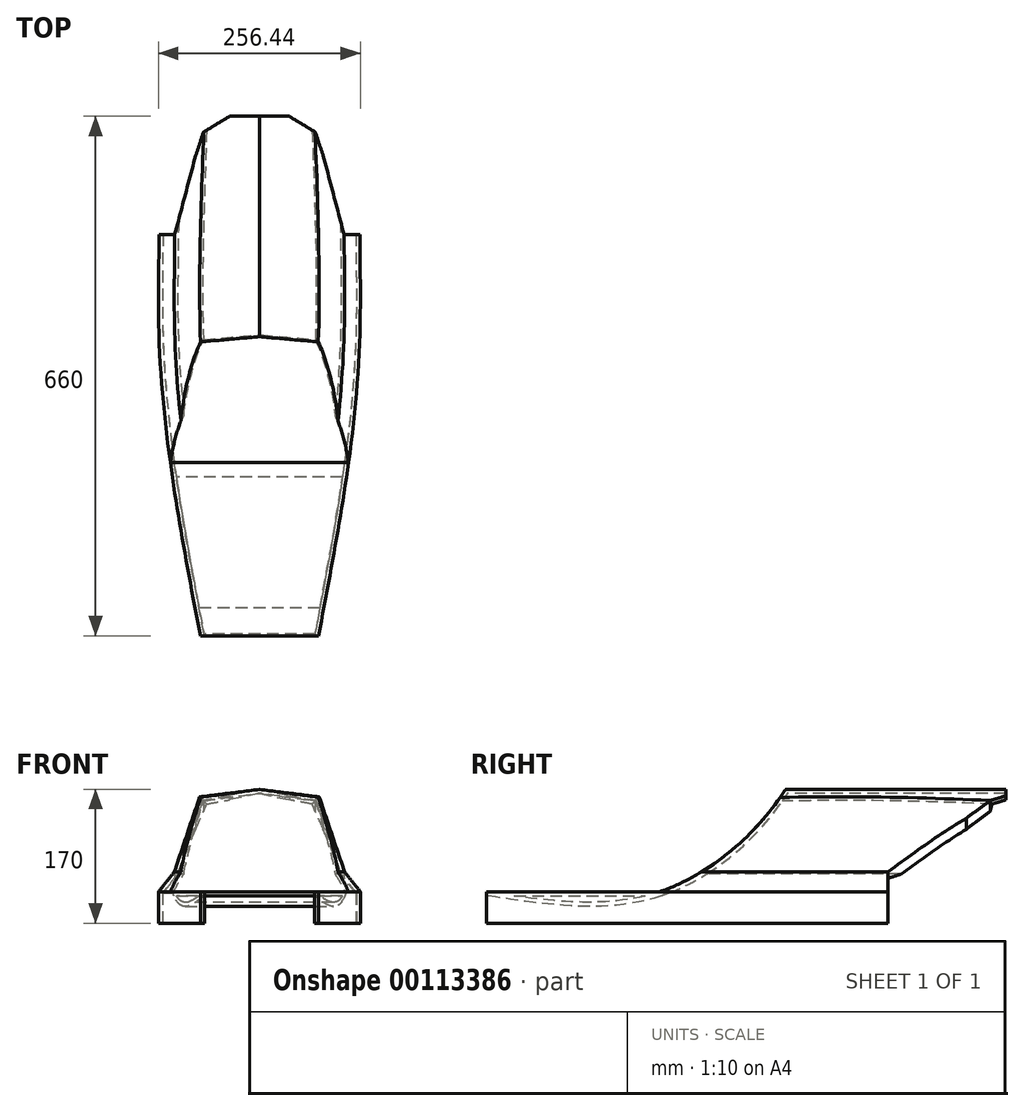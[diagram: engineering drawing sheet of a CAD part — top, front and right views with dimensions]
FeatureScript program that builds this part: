
annotation { "Feature Type Name" : "Feature", "Feature Type Description" : "" }
export const myFeature = defineFeature(function(context is Context, id is Id, definition is map)
    precondition{}
    {
        {
            var Q0;
            Q0=qCreatedBy(makeId("Front.planeOp"),FACE);
            cPlane(context, id + "F0", {"entities" : qUnion([Q0]), "cplaneType" : CPlaneType.OFFSET, "offset" : 380 * mm, "oppositeDirection" : true, "width" : 150 * mm, "height" : 150 * mm});
        }
        {
            var Q0;
            Q0=qCreatedBy(id+"F0.planeOp",FACE);
            cPlane(context, id + "F1", {"entities" : qUnion([Q0]), "cplaneType" : CPlaneType.OFFSET, "offset" : 130 * mm, "oppositeDirection" : true, "width" : 150 * mm, "height" : 150 * mm});
        }
        {
            var Q0;
            Q0=qCreatedBy(id+"F1.planeOp",FACE);
            cPlane(context, id + "F2", {"entities" : qUnion([Q0]), "cplaneType" : CPlaneType.OFFSET, "offset" : 150 * mm, "oppositeDirection" : true, "width" : 150 * mm, "height" : 150 * mm});
        }
        {
            var Q0;
            Q0=qCreatedBy(id+"F2.planeOp",FACE);
            var sketch = newSketch(context, id + "F3", { "sketchPlane" : qUnion([Q0])});
            skLineSegment(sketch, "E0.bottom", {"start": v(0, 0) * mm, "end": v(-127.5, 0) * mm, "construction": true});
            skLineSegment(sketch, "E0.top", {"start": v(0, 170) * mm, "end": v(-127.5, 170) * mm, "construction": true});
            skLineSegment(sketch, "E0.left", {"start": v(0, 0) * mm, "end": v(0, 170) * mm, "construction": true});
            skLineSegment(sketch, "E0.right", {"start": v(-127.5, 0) * mm, "end": v(-127.5, 170) * mm, "construction": true});
            skLineSegment(sketch, "E1.bottom", {"start": v(0, 170) * mm, "end": v(-70, 170) * mm, "construction": true});
            skLineSegment(sketch, "E1.top", {"start": v(0, 155) * mm, "end": v(-70, 155) * mm, "construction": true});
            skLineSegment(sketch, "E1.left", {"start": v(0, 170) * mm, "end": v(0, 155) * mm, "construction": true});
            skLineSegment(sketch, "E1.right", {"start": v(-70, 170) * mm, "end": v(-70, 155) * mm, "construction": true});
            skLineSegment(sketch, "E2.bottom", {"start": v(-127.5, 0) * mm, "end": v(-107.5, 0) * mm, "construction": true});
            skLineSegment(sketch, "E2.top", {"start": v(-127.5, 40) * mm, "end": v(-107.5, 40) * mm, "construction": true});
            skLineSegment(sketch, "E2.left", {"start": v(-127.5, 0) * mm, "end": v(-127.5, 40) * mm, "construction": true});
            skLineSegment(sketch, "E2.right", {"start": v(-107.5, 0) * mm, "end": v(-107.5, 40) * mm, "construction": true});
            skLineSegment(sketch, "E3.bottom", {"start": v(-107.5, 40) * mm, "end": v(-87.5, 40) * mm, "construction": true});
            skLineSegment(sketch, "E3.top", {"start": v(-107.5, 65) * mm, "end": v(-87.5, 65) * mm, "construction": true});
            skLineSegment(sketch, "E3.left", {"start": v(-107.5, 40) * mm, "end": v(-107.5, 65) * mm, "construction": true});
            skLineSegment(sketch, "E3.right", {"start": v(-87.5, 40) * mm, "end": v(-87.5, 65) * mm, "construction": true});
            skLineSegment(sketch, "E4", {"start": v(0, 170) * mm, "end": v(-70, 155) * mm});
            skLineSegment(sketch, "E5", {"start": v(-70, 155) * mm, "end": v(-107.5, 65) * mm});
            skLineSegment(sketch, "E6", {"start": v(-107.5, 65) * mm, "end": v(-127.5, 40) * mm});
            skLineSegment(sketch, "E7", {"start": v(-127.5, 40) * mm, "end": v(-127.5, 0) * mm});
            skLineSegment(sketch, "E8.MirrorCS", {"start": v(127.5, 0) * mm, "end": v(107.5, 0) * mm, "construction": true});
            skLineSegment(sketch, "E9.MirrorCS", {"start": v(127.5, 0) * mm, "end": v(127.5, 40) * mm, "construction": true});
            skLineSegment(sketch, "E10.MirrorCS", {"start": v(70, 170) * mm, "end": v(70, 155) * mm, "construction": true});
            skLineSegment(sketch, "E11.MirrorCS", {"start": v(0, 155) * mm, "end": v(70, 155) * mm, "construction": true});
            skLineSegment(sketch, "E12.MirrorCS", {"start": v(0, 170) * mm, "end": v(70, 170) * mm, "construction": true});
            skLineSegment(sketch, "E13.MirrorCS", {"start": v(127.5, 40) * mm, "end": v(107.5, 40) * mm, "construction": true});
            skLineSegment(sketch, "E14.MirrorCS", {"start": v(127.5, 0) * mm, "end": v(127.5, 170) * mm, "construction": true});
            skLineSegment(sketch, "E15.MirrorCS", {"start": v(0, 170) * mm, "end": v(127.5, 170) * mm, "construction": true});
            skLineSegment(sketch, "E16.MirrorCS", {"start": v(0, 0) * mm, "end": v(127.5, 0) * mm, "construction": true});
            skLineSegment(sketch, "E17.MirrorCS", {"start": v(87.5, 40) * mm, "end": v(87.5, 65) * mm, "construction": true});
            skLineSegment(sketch, "E18.MirrorCS", {"start": v(127.5, 40) * mm, "end": v(127.5, 0) * mm});
            skLineSegment(sketch, "E19.MirrorCS", {"start": v(107.5, 0) * mm, "end": v(107.5, 40) * mm, "construction": true});
            skLineSegment(sketch, "E20.MirrorCS", {"start": v(107.5, 40) * mm, "end": v(87.5, 40) * mm, "construction": true});
            skLineSegment(sketch, "E21.MirrorCS", {"start": v(0, 170) * mm, "end": v(70, 155) * mm});
            skLineSegment(sketch, "E22.MirrorCS", {"start": v(107.5, 40) * mm, "end": v(107.5, 65) * mm, "construction": true});
            skLineSegment(sketch, "E23.MirrorCS", {"start": v(107.5, 65) * mm, "end": v(87.5, 65) * mm, "construction": true});
            skLineSegment(sketch, "E24.MirrorCS", {"start": v(70, 155) * mm, "end": v(107.5, 65) * mm});
            skLineSegment(sketch, "E25.MirrorCS", {"start": v(107.5, 65) * mm, "end": v(127.5, 40) * mm});
            skLineSegment(sketch, "E26.0", {"start": v(122.5, 38.25) * mm, "end": v(122.5, 0) * mm});
            skLineSegment(sketch, "E26.1", {"start": v(103.16, 62.43) * mm, "end": v(122.5, 38.25) * mm});
            skLineSegment(sketch, "E26.2", {"start": v(66.4, 150.66) * mm, "end": v(103.16, 62.43) * mm});
            skLineSegment(sketch, "E26.3", {"start": v(0, 164.89) * mm, "end": v(66.4, 150.66) * mm});
            skLineSegment(sketch, "E26.4", {"start": v(-122.5, 38.25) * mm, "end": v(-122.5, 0) * mm});
            skLineSegment(sketch, "E26.5", {"start": v(-103.16, 62.43) * mm, "end": v(-122.5, 38.25) * mm});
            skLineSegment(sketch, "E26.6", {"start": v(-66.4, 150.66) * mm, "end": v(-103.16, 62.43) * mm});
            skLineSegment(sketch, "E26.7", {"start": v(0, 164.89) * mm, "end": v(-66.4, 150.66) * mm});
            skLineSegment(sketch, "E27", {"start": v(127.5, 0) * mm, "end": v(122.5, 0) * mm});
            skLineSegment(sketch, "E28", {"start": v(-122.5, 0) * mm, "end": v(-127.5, 0) * mm});
            skSolve(sketch);
        }
        {
            var Q0;
            Q0=qCreatedBy(id+"F1.planeOp",FACE);
            var sketch = newSketch(context, id + "F4", { "sketchPlane" : qUnion([Q0])});
            skLineSegment(sketch, "E29.bottom", {"start": v(0, 0) * mm, "end": v(-127.5, 0) * mm, "construction": true});
            skLineSegment(sketch, "E29.top", {"start": v(0, 170) * mm, "end": v(-127.5, 170) * mm, "construction": true});
            skLineSegment(sketch, "E29.left", {"start": v(0, 0) * mm, "end": v(0, 170) * mm, "construction": true});
            skLineSegment(sketch, "E29.right", {"start": v(-127.5, 0) * mm, "end": v(-127.5, 170) * mm, "construction": true});
            skLineSegment(sketch, "E30.bottom", {"start": v(0, 170) * mm, "end": v(-75, 170) * mm, "construction": true});
            skLineSegment(sketch, "E30.top", {"start": v(0, 160) * mm, "end": v(-75, 160) * mm, "construction": true});
            skLineSegment(sketch, "E30.left", {"start": v(0, 170) * mm, "end": v(0, 160) * mm, "construction": true});
            skLineSegment(sketch, "E30.right", {"start": v(-75, 170) * mm, "end": v(-75, 160) * mm, "construction": true});
            skLineSegment(sketch, "E31.bottom", {"start": v(-127.5, 0) * mm, "end": v(-107.5, 0) * mm, "construction": true});
            skLineSegment(sketch, "E31.top", {"start": v(-127.5, 40) * mm, "end": v(-107.5, 40) * mm, "construction": true});
            skLineSegment(sketch, "E31.left", {"start": v(-127.5, 0) * mm, "end": v(-127.5, 40) * mm, "construction": true});
            skLineSegment(sketch, "E31.right", {"start": v(-107.5, 0) * mm, "end": v(-107.5, 40) * mm, "construction": true});
            skLineSegment(sketch, "E32.bottom", {"start": v(-107.5, 40) * mm, "end": v(-87.5, 40) * mm, "construction": true});
            skLineSegment(sketch, "E32.top", {"start": v(-107.5, 65) * mm, "end": v(-87.5, 65) * mm, "construction": true});
            skLineSegment(sketch, "E32.left", {"start": v(-107.5, 40) * mm, "end": v(-107.5, 65) * mm, "construction": true});
            skLineSegment(sketch, "E32.right", {"start": v(-87.5, 40) * mm, "end": v(-87.5, 65) * mm, "construction": true});
            skLineSegment(sketch, "E33", {"start": v(0, 170) * mm, "end": v(-75, 160) * mm});
            skLineSegment(sketch, "E34", {"start": v(-75, 160) * mm, "end": v(-107.5, 65) * mm});
            skLineSegment(sketch, "E35", {"start": v(-107.5, 65) * mm, "end": v(-127.5, 40) * mm});
            skLineSegment(sketch, "E36", {"start": v(-127.5, 40) * mm, "end": v(-127.5, 0) * mm});
            skLineSegment(sketch, "E37.MirrorCS", {"start": v(127.5, 0) * mm, "end": v(107.5, 0) * mm, "construction": true});
            skLineSegment(sketch, "E38.MirrorCS", {"start": v(127.5, 0) * mm, "end": v(127.5, 40) * mm, "construction": true});
            skLineSegment(sketch, "E39.MirrorCS", {"start": v(75, 170) * mm, "end": v(75, 160) * mm, "construction": true});
            skLineSegment(sketch, "E40.MirrorCS", {"start": v(0, 160) * mm, "end": v(75, 160) * mm, "construction": true});
            skLineSegment(sketch, "E41.MirrorCS", {"start": v(0, 170) * mm, "end": v(75, 170) * mm, "construction": true});
            skLineSegment(sketch, "E42.MirrorCS", {"start": v(127.5, 40) * mm, "end": v(107.5, 40) * mm, "construction": true});
            skLineSegment(sketch, "E43.MirrorCS", {"start": v(127.5, 0) * mm, "end": v(127.5, 170) * mm, "construction": true});
            skLineSegment(sketch, "E44.MirrorCS", {"start": v(0, 170) * mm, "end": v(127.5, 170) * mm, "construction": true});
            skLineSegment(sketch, "E45.MirrorCS", {"start": v(0, 0) * mm, "end": v(127.5, 0) * mm, "construction": true});
            skLineSegment(sketch, "E46.MirrorCS", {"start": v(87.5, 40) * mm, "end": v(87.5, 65) * mm, "construction": true});
            skLineSegment(sketch, "E47.MirrorCS", {"start": v(127.5, 40) * mm, "end": v(127.5, 0) * mm});
            skLineSegment(sketch, "E48.MirrorCS", {"start": v(107.5, 0) * mm, "end": v(107.5, 40) * mm, "construction": true});
            skLineSegment(sketch, "E49.MirrorCS", {"start": v(107.5, 40) * mm, "end": v(87.5, 40) * mm, "construction": true});
            skLineSegment(sketch, "E50.MirrorCS", {"start": v(0, 170) * mm, "end": v(75, 160) * mm});
            skLineSegment(sketch, "E51.MirrorCS", {"start": v(107.5, 40) * mm, "end": v(107.5, 65) * mm, "construction": true});
            skLineSegment(sketch, "E52.MirrorCS", {"start": v(107.5, 65) * mm, "end": v(87.5, 65) * mm, "construction": true});
            skLineSegment(sketch, "E53.MirrorCS", {"start": v(75, 160) * mm, "end": v(107.5, 65) * mm});
            skLineSegment(sketch, "E54.MirrorCS", {"start": v(107.5, 65) * mm, "end": v(127.5, 40) * mm});
            skLineSegment(sketch, "E55.0", {"start": v(122.5, 38.25) * mm, "end": v(122.5, 0) * mm});
            skLineSegment(sketch, "E55.1", {"start": v(103.05, 62.56) * mm, "end": v(122.5, 38.25) * mm});
            skLineSegment(sketch, "E55.2", {"start": v(71.27, 155.45) * mm, "end": v(103.05, 62.56) * mm});
            skLineSegment(sketch, "E55.3", {"start": v(0, 164.96) * mm, "end": v(71.27, 155.45) * mm});
            skLineSegment(sketch, "E55.4", {"start": v(-122.5, 38.25) * mm, "end": v(-122.5, 0) * mm});
            skLineSegment(sketch, "E55.5", {"start": v(-103.05, 62.56) * mm, "end": v(-122.5, 38.25) * mm});
            skLineSegment(sketch, "E55.6", {"start": v(-71.27, 155.45) * mm, "end": v(-103.05, 62.56) * mm});
            skLineSegment(sketch, "E55.7", {"start": v(0, 164.96) * mm, "end": v(-71.27, 155.45) * mm});
            skLineSegment(sketch, "E56", {"start": v(127.5, 0) * mm, "end": v(122.5, 0) * mm});
            skLineSegment(sketch, "E57", {"start": v(-122.5, 0) * mm, "end": v(-127.5, 0) * mm});
            skSolve(sketch);
        }
        {
            var Q0;
            Q0=qCreatedBy(id+"F0.planeOp",FACE);
            var sketch = newSketch(context, id + "F5", { "sketchPlane" : qUnion([Q0])});
            skLineSegment(sketch, "E58.bottom", {"start": v(0, 0) * mm, "end": v(-127.5, 0) * mm, "construction": true});
            skLineSegment(sketch, "E58.top", {"start": v(0, 170) * mm, "end": v(-127.5, 170) * mm, "construction": true});
            skLineSegment(sketch, "E58.left", {"start": v(0, 0) * mm, "end": v(0, 170) * mm, "construction": true});
            skLineSegment(sketch, "E58.right", {"start": v(-127.5, 0) * mm, "end": v(-127.5, 170) * mm, "construction": true});
            skLineSegment(sketch, "E59.bottom", {"start": v(0, 170) * mm, "end": v(-75, 170) * mm, "construction": true});
            skLineSegment(sketch, "E59.top", {"start": v(0, 160) * mm, "end": v(-75, 160) * mm, "construction": true});
            skLineSegment(sketch, "E59.left", {"start": v(0, 170) * mm, "end": v(0, 160) * mm, "construction": true});
            skLineSegment(sketch, "E59.right", {"start": v(-75, 170) * mm, "end": v(-75, 160) * mm, "construction": true});
            skLineSegment(sketch, "E60.bottom", {"start": v(-127.5, 0) * mm, "end": v(-107.5, 0) * mm, "construction": true});
            skLineSegment(sketch, "E60.top", {"start": v(-127.5, 40) * mm, "end": v(-107.5, 40) * mm, "construction": true});
            skLineSegment(sketch, "E60.left", {"start": v(-127.5, 0) * mm, "end": v(-127.5, 40) * mm, "construction": true});
            skLineSegment(sketch, "E60.right", {"start": v(-107.5, 0) * mm, "end": v(-107.5, 40) * mm, "construction": true});
            skLineSegment(sketch, "E61.bottom", {"start": v(-107.5, 40) * mm, "end": v(-87.5, 40) * mm, "construction": true});
            skLineSegment(sketch, "E61.top", {"start": v(-107.5, 65) * mm, "end": v(-87.5, 65) * mm, "construction": true});
            skLineSegment(sketch, "E61.left", {"start": v(-107.5, 40) * mm, "end": v(-107.5, 65) * mm, "construction": true});
            skLineSegment(sketch, "E61.right", {"start": v(-87.5, 40) * mm, "end": v(-87.5, 65) * mm, "construction": true});
            skLineSegment(sketch, "E62", {"start": v(0, 170) * mm, "end": v(-75, 160) * mm});
            skLineSegment(sketch, "E63", {"start": v(-75, 160) * mm, "end": v(-107.5, 65) * mm});
            skLineSegment(sketch, "E64", {"start": v(-107.5, 65) * mm, "end": v(-127.5, 40) * mm});
            skLineSegment(sketch, "E65", {"start": v(-127.5, 40) * mm, "end": v(-127.5, 0) * mm});
            skLineSegment(sketch, "E66.MirrorCS", {"start": v(127.5, 0) * mm, "end": v(107.5, 0) * mm, "construction": true});
            skLineSegment(sketch, "E67.MirrorCS", {"start": v(127.5, 0) * mm, "end": v(127.5, 40) * mm, "construction": true});
            skLineSegment(sketch, "E68.MirrorCS", {"start": v(75, 170) * mm, "end": v(75, 160) * mm, "construction": true});
            skLineSegment(sketch, "E69.MirrorCS", {"start": v(0, 160) * mm, "end": v(75, 160) * mm, "construction": true});
            skLineSegment(sketch, "E70.MirrorCS", {"start": v(0, 170) * mm, "end": v(75, 170) * mm, "construction": true});
            skLineSegment(sketch, "E71.MirrorCS", {"start": v(127.5, 40) * mm, "end": v(107.5, 40) * mm, "construction": true});
            skLineSegment(sketch, "E72.MirrorCS", {"start": v(127.5, 0) * mm, "end": v(127.5, 170) * mm, "construction": true});
            skLineSegment(sketch, "E73.MirrorCS", {"start": v(0, 170) * mm, "end": v(127.5, 170) * mm, "construction": true});
            skLineSegment(sketch, "E74.MirrorCS", {"start": v(0, 0) * mm, "end": v(127.5, 0) * mm, "construction": true});
            skLineSegment(sketch, "E75.MirrorCS", {"start": v(87.5, 40) * mm, "end": v(87.5, 65) * mm, "construction": true});
            skLineSegment(sketch, "E76.MirrorCS", {"start": v(127.5, 40) * mm, "end": v(127.5, 0) * mm});
            skLineSegment(sketch, "E77.MirrorCS", {"start": v(107.5, 0) * mm, "end": v(107.5, 40) * mm, "construction": true});
            skLineSegment(sketch, "E78.MirrorCS", {"start": v(107.5, 40) * mm, "end": v(87.5, 40) * mm, "construction": true});
            skLineSegment(sketch, "E79.MirrorCS", {"start": v(0, 170) * mm, "end": v(75, 160) * mm});
            skLineSegment(sketch, "E80.MirrorCS", {"start": v(107.5, 40) * mm, "end": v(107.5, 65) * mm, "construction": true});
            skLineSegment(sketch, "E81.MirrorCS", {"start": v(107.5, 65) * mm, "end": v(87.5, 65) * mm, "construction": true});
            skLineSegment(sketch, "E82.MirrorCS", {"start": v(75, 160) * mm, "end": v(107.5, 65) * mm});
            skLineSegment(sketch, "E83.MirrorCS", {"start": v(107.5, 65) * mm, "end": v(127.5, 40) * mm});
            skLineSegment(sketch, "E84.0", {"start": v(122.5, 38.25) * mm, "end": v(122.5, 0) * mm});
            skLineSegment(sketch, "E84.1", {"start": v(103.05, 62.56) * mm, "end": v(122.5, 38.25) * mm});
            skLineSegment(sketch, "E84.2", {"start": v(71.27, 155.45) * mm, "end": v(103.05, 62.56) * mm});
            skLineSegment(sketch, "E84.3", {"start": v(0, 164.96) * mm, "end": v(71.27, 155.45) * mm});
            skLineSegment(sketch, "E84.4", {"start": v(-122.5, 38.25) * mm, "end": v(-122.5, 0) * mm});
            skLineSegment(sketch, "E84.5", {"start": v(-103.05, 62.56) * mm, "end": v(-122.5, 38.25) * mm});
            skLineSegment(sketch, "E84.6", {"start": v(-71.27, 155.45) * mm, "end": v(-103.05, 62.56) * mm});
            skLineSegment(sketch, "E84.7", {"start": v(0, 164.96) * mm, "end": v(-71.27, 155.45) * mm});
            skLineSegment(sketch, "E85", {"start": v(127.5, 0) * mm, "end": v(122.5, 0) * mm});
            skLineSegment(sketch, "E86", {"start": v(-122.5, 0) * mm, "end": v(-127.5, 0) * mm});
            skSolve(sketch);
        }
        {
            var Q0;
            Q0=qCreatedBy(makeId("Front.planeOp"),FACE);
            var sketch = newSketch(context, id + "F6", { "sketchPlane" : qUnion([Q0])});
            skLineSegment(sketch, "E87.bottom", {"start": v(0, 0) * mm, "end": v(-75, 0) * mm, "construction": true});
            skLineSegment(sketch, "E87.top", {"start": v(0, 170) * mm, "end": v(-75, 170) * mm, "construction": true});
            skLineSegment(sketch, "E87.left", {"start": v(0, 0) * mm, "end": v(0, 170) * mm, "construction": true});
            skLineSegment(sketch, "E87.right", {"start": v(-75, 0) * mm, "end": v(-75, 170) * mm, "construction": true});
            skLineSegment(sketch, "E88.bottom", {"start": v(0, 170) * mm, "end": v(-30, 170) * mm, "construction": true});
            skLineSegment(sketch, "E88.top", {"start": v(0, 160) * mm, "end": v(-30, 160) * mm, "construction": true});
            skLineSegment(sketch, "E88.left", {"start": v(0, 170) * mm, "end": v(0, 160) * mm, "construction": true});
            skLineSegment(sketch, "E88.right", {"start": v(-30, 170) * mm, "end": v(-30, 160) * mm, "construction": true});
            skLineSegment(sketch, "E89.bottom", {"start": v(-75, 0) * mm, "end": v(-55, 0) * mm, "construction": true});
            skLineSegment(sketch, "E89.top", {"start": v(-75, 40) * mm, "end": v(-55, 40) * mm, "construction": true});
            skLineSegment(sketch, "E89.left", {"start": v(-75, 0) * mm, "end": v(-75, 40) * mm, "construction": true});
            skLineSegment(sketch, "E89.right", {"start": v(-55, 0) * mm, "end": v(-55, 40) * mm, "construction": true});
            skLineSegment(sketch, "E90.bottom", {"start": v(-55, 40) * mm, "end": v(-35, 40) * mm, "construction": true});
            skLineSegment(sketch, "E90.top", {"start": v(-55, 65) * mm, "end": v(-35, 65) * mm, "construction": true});
            skLineSegment(sketch, "E90.left", {"start": v(-55, 40) * mm, "end": v(-55, 65) * mm, "construction": true});
            skLineSegment(sketch, "E90.right", {"start": v(-35, 40) * mm, "end": v(-35, 65) * mm, "construction": true});
            skLineSegment(sketch, "E91", {"start": v(0, 170) * mm, "end": v(-30, 160) * mm});
            skLineSegment(sketch, "E92", {"start": v(-30, 160) * mm, "end": v(-55, 65) * mm});
            skLineSegment(sketch, "E93", {"start": v(-55, 65) * mm, "end": v(-75, 40) * mm});
            skLineSegment(sketch, "E94", {"start": v(-75, 40) * mm, "end": v(-75, 0) * mm});
            skLineSegment(sketch, "E95.MirrorCS", {"start": v(75, 0) * mm, "end": v(55, 0) * mm, "construction": true});
            skLineSegment(sketch, "E96.MirrorCS", {"start": v(75, 0) * mm, "end": v(75, 40) * mm, "construction": true});
            skLineSegment(sketch, "E97.MirrorCS", {"start": v(30, 170) * mm, "end": v(30, 160) * mm, "construction": true});
            skLineSegment(sketch, "E98.MirrorCS", {"start": v(0, 160) * mm, "end": v(30, 160) * mm, "construction": true});
            skLineSegment(sketch, "E99.MirrorCS", {"start": v(0, 170) * mm, "end": v(30, 170) * mm, "construction": true});
            skLineSegment(sketch, "E100.MirrorCS", {"start": v(75, 40) * mm, "end": v(55, 40) * mm, "construction": true});
            skLineSegment(sketch, "E101.MirrorCS", {"start": v(75, 0) * mm, "end": v(75, 170) * mm, "construction": true});
            skLineSegment(sketch, "E102.MirrorCS", {"start": v(0, 170) * mm, "end": v(75, 170) * mm, "construction": true});
            skLineSegment(sketch, "E103.MirrorCS", {"start": v(0, 0) * mm, "end": v(75, 0) * mm, "construction": true});
            skLineSegment(sketch, "E104.MirrorCS", {"start": v(35, 40) * mm, "end": v(35, 65) * mm, "construction": true});
            skLineSegment(sketch, "E105.MirrorCS", {"start": v(75, 40) * mm, "end": v(75, 0) * mm});
            skLineSegment(sketch, "E106.MirrorCS", {"start": v(55, 0) * mm, "end": v(55, 40) * mm, "construction": true});
            skLineSegment(sketch, "E107.MirrorCS", {"start": v(55, 40) * mm, "end": v(35, 40) * mm, "construction": true});
            skLineSegment(sketch, "E108.MirrorCS", {"start": v(0, 170) * mm, "end": v(30, 160) * mm});
            skLineSegment(sketch, "E109.MirrorCS", {"start": v(55, 40) * mm, "end": v(55, 65) * mm, "construction": true});
            skLineSegment(sketch, "E110.MirrorCS", {"start": v(55, 65) * mm, "end": v(35, 65) * mm, "construction": true});
            skLineSegment(sketch, "E111.MirrorCS", {"start": v(30, 160) * mm, "end": v(55, 65) * mm});
            skLineSegment(sketch, "E112.MirrorCS", {"start": v(55, 65) * mm, "end": v(75, 40) * mm});
            skLineSegment(sketch, "E113.0", {"start": v(70, 38.25) * mm, "end": v(70, 0) * mm});
            skLineSegment(sketch, "E113.1", {"start": v(50.43, 62.7) * mm, "end": v(70, 38.25) * mm});
            skLineSegment(sketch, "E113.2", {"start": v(25.85, 156.11) * mm, "end": v(50.43, 62.7) * mm});
            skLineSegment(sketch, "E113.3", {"start": v(0, 164.73) * mm, "end": v(25.85, 156.11) * mm});
            skLineSegment(sketch, "E113.4", {"start": v(-70, 38.25) * mm, "end": v(-70, 0) * mm});
            skLineSegment(sketch, "E113.5", {"start": v(-50.43, 62.7) * mm, "end": v(-70, 38.25) * mm});
            skLineSegment(sketch, "E113.6", {"start": v(-25.85, 156.11) * mm, "end": v(-50.43, 62.7) * mm});
            skLineSegment(sketch, "E113.7", {"start": v(0, 164.73) * mm, "end": v(-25.85, 156.11) * mm});
            skLineSegment(sketch, "E114", {"start": v(75, 0) * mm, "end": v(70, 0) * mm});
            skLineSegment(sketch, "E115", {"start": v(-70, 0) * mm, "end": v(-75, 0) * mm});
            skSolve(sketch);
        }
        {
            var Q0;
            Q0=qCreatedBy(makeId("Right.planeOp"),FACE);
            var sketch = newSketch(context, id + "F7", { "sketchPlane" : qUnion([Q0])});
            skLineSegment(sketch, "E116", {"start": v(0, 0) * mm, "end": v(380, 0) * mm, "construction": true});
            skLineSegment(sketch, "E117", {"start": v(380, 0) * mm, "end": v(380, 170) * mm, "construction": true});
            skLineSegment(sketch, "E118", {"start": v(0, 0) * mm, "end": v(0, 40) * mm, "construction": true});
            skLineSegment(sketch, "E119", {"start": v(0, 40) * mm, "end": v(220, 40) * mm});
            skFitSpline(sketch, "E120", {"points": [v(380, 170) * mm, v(220, 40) * mm, v(0, 40) * mm], "startDerivative": vector(-215.96, -343.22) * mm, "endDerivative": vector(-478.3, 74.11) * mm});
            skLineSegment(sketch, "E121", {"start": v(380, 170) * mm, "end": v(380, 230.78) * mm});
            skLineSegment(sketch, "E122", {"start": v(380, 230.78) * mm, "end": v(7.34, 230.78) * mm});
            skLineSegment(sketch, "E123", {"start": v(7.34, 230.78) * mm, "end": v(-5.55, 185.11) * mm});
            skLineSegment(sketch, "E124", {"start": v(-5.55, 185.11) * mm, "end": v(0, 40) * mm});
            skSolve(sketch);
        }
        {
            var Q0;
            Q0=qCreatedBy(makeId("Right.planeOp"),FACE);
            var sketch = newSketch(context, id + "F8", { "sketchPlane" : qUnion([Q0])});
            skLineSegment(sketch, "E125", {"start": v(0, 0) * mm, "end": v(600, 0) * mm, "construction": true});
            skLineSegment(sketch, "E126", {"start": v(600, 0) * mm, "end": v(600, 40) * mm});
            skLineSegment(sketch, "E127", {"start": v(600, 40) * mm, "end": v(600, 65) * mm, "construction": true});
            skLineSegment(sketch, "E128", {"start": v(600, 65) * mm, "end": v(625, 65) * mm, "construction": true});
            skLineSegment(sketch, "E129", {"start": v(600, 40) * mm, "end": v(625, 65) * mm});
            skLineSegment(sketch, "E130", {"start": v(625, 65) * mm, "end": v(880.62, 212.2) * mm});
            skLineSegment(sketch, "E131", {"start": v(880.62, 212.2) * mm, "end": v(932.67, 242.1) * mm});
            skLineSegment(sketch, "E132", {"start": v(932.67, 242.1) * mm, "end": v(866.28, 117.59) * mm});
            skLineSegment(sketch, "E133", {"start": v(866.28, 117.59) * mm, "end": v(834.8, 61.75) * mm});
            skLineSegment(sketch, "E134", {"start": v(600, 0) * mm, "end": v(790, 0) * mm});
            skLineSegment(sketch, "E135", {"start": v(790, 0) * mm, "end": v(790, 65) * mm, "construction": true});
            skLineSegment(sketch, "E136", {"start": v(834.8, 61.75) * mm, "end": v(790, 0) * mm});
            skSolve(sketch);
        }
        {
            var Q0;
            Q0=qCreatedBy(makeId("Right.planeOp"),FACE);
            var sketch = newSketch(context, id + "F9", { "sketchPlane" : qUnion([Q0])});
            skLineSegment(sketch, "E137", {"start": v(0, 0) * mm, "end": v(380, 0) * mm, "construction": true});
            skLineSegment(sketch, "E138", {"start": v(380, 0) * mm, "end": v(380, 170) * mm, "construction": true});
            skLineSegment(sketch, "E139", {"start": v(0, 0) * mm, "end": v(0, 40) * mm, "construction": true});
            skLineSegment(sketch, "E140", {"start": v(0, 40) * mm, "end": v(220, 40) * mm});
            skFitSpline(sketch, "E141", {"points": [v(380, 170) * mm, v(220, 40) * mm, v(0, 40) * mm], "startDerivative": vector(-215.96, -343.22) * mm, "endDerivative": vector(-478.3, 74.11) * mm});
            skLineSegment(sketch, "E142", {"start": v(2.2, -5.3) * mm, "end": v(382.2, -5.3) * mm, "construction": true});
            skLineSegment(sketch, "E143", {"start": v(382.2, -5.3) * mm, "end": v(382.2, 164.7) * mm, "construction": true});
            skLineSegment(sketch, "E144", {"start": v(2.2, -5.3) * mm, "end": v(2.2, 34.7) * mm, "construction": true});
            skLineSegment(sketch, "E145", {"start": v(2.2, 34.7) * mm, "end": v(222.2, 34.7) * mm});
            skFitSpline(sketch, "E146", {"points": [v(382.2, 164.7) * mm, v(222.2, 34.7) * mm, v(2.2, 34.7) * mm], "startDerivative": vector(-215.96, -343.22) * mm, "endDerivative": vector(-478.3, 74.11) * mm});
            skLineSegment(sketch, "E147", {"start": v(2.2, 34.7) * mm, "end": v(0, 40) * mm});
            skLineSegment(sketch, "E148", {"start": v(382.2, 164.7) * mm, "end": v(380, 170) * mm});
            skSolve(sketch);
        }
        {
            var Q0;
            Q0 = qSketchRegion(id + "F3", true);
            var Q1;
            Q1 = qSketchRegion(id + "F4", true);
            var Q2;
            Q2 = qSketchRegion(id + "F5", true);
            var Q3;
            Q3 = qSketchRegion(id + "F6", true);
            loft(context, id + "F10", {"sheetProfilesArray" : [{ "sheetProfileEntities" : qUnion([Q0]) }, { "sheetProfileEntities" : qUnion([Q1]) }, { "sheetProfileEntities" : qUnion([Q2]) }, { "sheetProfileEntities" : qUnion([Q3]) }]});
        }
        {
            var Q0;
            Q0=makeQuery(id+"F7.imprint","IMPRINT",FACE,{"disambiguationData":[TD([[makeQuery(id+"F7.imprint","IMPRINT",EDGE,{"derivedFrom":sQuery(id+"F7.wireOp",EDGE,"E119")}),1.0]])]});
            extrude(context, id + "F11", {"entities" : qUnion([Q0]), "operationType" : NewBodyOperationType.REMOVE, "endBound" : BoundingType.THROUGH_ALL, "oppositeDirection" : true, "depth" : 25 * mm, "hasSecondDirection" : true, "secondDirectionBound" : SecondDirectionBoundingType.THROUGH_ALL, "secondDirectionOppositeDirection" : false, "secondDirectionDepth" : 25 * mm});
        }
        {
            var Q0;
            Q0 = qSketchRegion(id + "F9", true);
            var Q1;
            Q1 = qConstructionFilter(qBodyType(qCreatedBy(id + "F6" ,EDGE), BodyType.WIRE), ConstructionObject.NO);
            var Q2;
            Q2 = qConstructionFilter(qBodyType(qCreatedBy(id + "F5" ,EDGE), BodyType.WIRE), ConstructionObject.NO);
            var Q3;
            Q3 = qConstructionFilter(qBodyType(qCreatedBy(id + "F4" ,EDGE), BodyType.WIRE), ConstructionObject.NO);
            var Q4;
            Q4=makeQuery(id+"F10.opLoft","SWEPT_BODY",BODY,{"disambiguationData":[OSD([makeQuery(id+"F3.imprint","IMPRINT",FACE,{"disambiguationData":[TD([[makeQuery(id+"F3.imprint","IMPRINT",EDGE,{"derivedFrom":sQuery(id+"F3.wireOp",EDGE,"E4")}),1.0]])]}),sQuery(id+"F4.wireOp",EDGE,"E55.7"),sQuery(id+"F5.wireOp",EDGE,"E84.7"),makeQuery(id+"F6.imprint","IMPRINT",FACE,{"disambiguationData":[TD([[makeQuery(id+"F6.imprint","IMPRINT",EDGE,{"derivedFrom":sQuery(id+"F6.wireOp",EDGE,"E91")}),1.0]])]})])]});
            var Q5;
            Q5=makeQuery(id+"F10.opLoft","SWEPT_BODY",BODY,{"disambiguationData":[OSD([makeQuery(id+"F3.imprint","IMPRINT",FACE,{"disambiguationData":[TD([[makeQuery(id+"F3.imprint","IMPRINT",EDGE,{"derivedFrom":sQuery(id+"F3.wireOp",EDGE,"E4")}),1.0]])]}),sQuery(id+"F4.wireOp",EDGE,"E55.7"),sQuery(id+"F5.wireOp",EDGE,"E84.7"),makeQuery(id+"F6.imprint","IMPRINT",FACE,{"disambiguationData":[TD([[makeQuery(id+"F6.imprint","IMPRINT",EDGE,{"derivedFrom":sQuery(id+"F6.wireOp",EDGE,"E91")}),1.0]])]})])]});
            extrude(context, id + "F12", {"entities" : qUnion([Q0]), "operationType" : NewBodyOperationType.ADD, "surfaceEntities" : qUnion([Q1, Q2, Q3]), "endBound" : BoundingType.UP_TO_BODY, "endBoundEntityBody" : qUnion([Q4]), "depth" : 170 * mm, "hasSecondDirection" : true, "secondDirectionBound" : SecondDirectionBoundingType.UP_TO_BODY, "secondDirectionOppositeDirection" : true, "secondDirectionBoundEntityBody" : qUnion([Q5]), "secondDirectionDepth" : 25 * mm});
        }
        {
            var Q0;
            Q0=qCreatedBy(makeId("Top.planeOp"),FACE);
            var sketch = newSketch(context, id + "F13", { "sketchPlane" : qUnion([Q0])});
            skLineSegment(sketch, "E149", {"start": v(0, 0) * mm, "end": v(0, 660) * mm, "construction": true});
            skLineSegment(sketch, "E150", {"start": v(0, 660) * mm, "end": v(-38, 660) * mm, "construction": true});
            skLineSegment(sketch, "E151", {"start": v(0, 640) * mm, "end": v(-71, 640) * mm, "construction": true});
            skLineSegment(sketch, "E152", {"start": v(-38, 660) * mm, "end": v(-71, 640) * mm});
            skLineSegment(sketch, "E153", {"start": v(-71, 640) * mm, "end": v(-71, 610) * mm, "construction": true});
            skLineSegment(sketch, "E154", {"start": v(-71, 610) * mm, "end": v(-81, 610) * mm, "construction": true});
            skLineSegment(sketch, "E155", {"start": v(-71, 640) * mm, "end": v(-81, 610) * mm});
            skLineSegment(sketch, "E156", {"start": v(-81, 610) * mm, "end": v(-81, 605) * mm, "construction": true});
            skLineSegment(sketch, "E157", {"start": v(0, 510) * mm, "end": v(-107.58, 510) * mm, "construction": true});
            skLineSegment(sketch, "E158", {"start": v(-81, 610) * mm, "end": v(-107.58, 510) * mm});
            skLineSegment(sketch, "E159", {"start": v(-107.58, 510) * mm, "end": v(-166.67, 510) * mm});
            skLineSegment(sketch, "E160", {"start": v(-166.67, 510) * mm, "end": v(-157.39, 706.64) * mm});
            skLineSegment(sketch, "E161", {"start": v(-157.39, 706.64) * mm, "end": v(-38, 660) * mm});
            skLineSegment(sketch, "E162.MirrorCS", {"start": v(81, 610) * mm, "end": v(81, 610) * mm});
            skLineSegment(sketch, "E163.MirrorCS", {"start": v(81, 610) * mm, "end": v(81, 605) * mm, "construction": true});
            skLineSegment(sketch, "E164.MirrorCS", {"start": v(81, 605) * mm, "end": v(81, 610) * mm, "construction": true});
            skLineSegment(sketch, "E165.MirrorCS", {"start": v(71, 610) * mm, "end": v(81, 610) * mm, "construction": true});
            skLineSegment(sketch, "E166.MirrorCS", {"start": v(71, 640) * mm, "end": v(71, 610) * mm, "construction": true});
            skLineSegment(sketch, "E167.MirrorCS", {"start": v(0, 660) * mm, "end": v(38, 660) * mm, "construction": true});
            skLineSegment(sketch, "E168.MirrorCS", {"start": v(71, 640) * mm, "end": v(81, 610) * mm});
            skLineSegment(sketch, "E169.MirrorCS", {"start": v(166.67, 510) * mm, "end": v(157.39, 706.64) * mm});
            skLineSegment(sketch, "E170.MirrorCS", {"start": v(0, 640) * mm, "end": v(71, 640) * mm, "construction": true});
            skLineSegment(sketch, "E171.MirrorCS", {"start": v(0, 510) * mm, "end": v(107.58, 510) * mm, "construction": true});
            skLineSegment(sketch, "E172.MirrorCS", {"start": v(38, 660) * mm, "end": v(71, 640) * mm});
            skLineSegment(sketch, "E173.MirrorCS", {"start": v(81, 610) * mm, "end": v(107.58, 510) * mm});
            skLineSegment(sketch, "E174.MirrorCS", {"start": v(157.39, 706.64) * mm, "end": v(38, 660) * mm});
            skLineSegment(sketch, "E175.MirrorCS", {"start": v(107.58, 510) * mm, "end": v(166.67, 510) * mm});
            skSolve(sketch);
        }
        {
            var Q0;
            Q0 = qSketchRegion(id + "F13", true);
            var Q1;
            Q1=makeQuery(id+"F10.opLoft","SWEPT_BODY",BODY,{"disambiguationData":[OSD([makeQuery(id+"F3.imprint","IMPRINT",FACE,{"disambiguationData":[TD([[makeQuery(id+"F3.imprint","IMPRINT",EDGE,{"derivedFrom":sQuery(id+"F3.wireOp",EDGE,"E4")}),1.0]])]}),sQuery(id+"F4.wireOp",EDGE,"E55.7"),sQuery(id+"F5.wireOp",EDGE,"E84.7"),makeQuery(id+"F6.imprint","IMPRINT",FACE,{"disambiguationData":[TD([[makeQuery(id+"F6.imprint","IMPRINT",EDGE,{"derivedFrom":sQuery(id+"F6.wireOp",EDGE,"E91")}),1.0]])]})])]});
            extrude(context, id + "F14", {"entities" : qUnion([Q0]), "operationType" : NewBodyOperationType.REMOVE, "endBound" : BoundingType.UP_TO_BODY, "endBoundEntityBody" : qUnion([Q1]), "depth" : 25 * mm});
        }
    });
